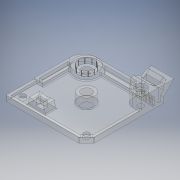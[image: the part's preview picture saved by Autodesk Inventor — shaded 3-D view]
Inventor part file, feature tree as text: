
AUTODESK INVENTOR PART (.ipt)
format: ipt  version: 2017 (Build 210142000, 142)  size: 582,144 bytes
history: native  units: in
note: dims shown in document units (in); Inventor stores cm internally (conversion verified against a paired STEP export)
features: extrude x21, sketch x21, projected_geometry x5, chamfer x3, fillet x3, pattern_circular x1
ambient origin geometry x8: Origin, YZ Plane, XZ Plane, XY Plane, X Axis, Y Axis, Z Axis, Center Point
bodies: Solid1 (feature_tree)
feature tree (54):
  extrude  "Extrusion1"  Depth=1.7323in
  chamfer  "Chamfer2"  Distance=0.1181in
  extrude  "Extrusion2"  Depth=0.1772in TaperAngle=45.0deg
  extrude  "Extrusion3"  Depth=0.1969in
  extrude  "Extrusion4"  Depth=0.815in
  extrude  "Extrusion5"  Depth=0.5118in
  extrude  "Extrusion6"  Depth=0.0787in
  fillet  "Fillet3"  Radius=0.1142in
  pattern_circular  "Circular Pattern1"  Count=10 Angle=360.0deg
  fillet  "Fillet4"  Radius=0.2953in
  extrude  "Extrusion7"  Depth=0.0591in
  extrude  "Extrusion8"  Depth=0.0591in
  extrude  "Extrusion9"  Depth=0.0394in
  extrude  "Extrusion10"  Depth=0.0984in
  extrude  "Extrusion11"  Depth=0.0591in
  chamfer  "Chamfer3"  Distance=0.0591in
  chamfer  "Chamfer4"  Distance=0.0591in
  extrude  "Extrusion12"  Depth=0.0591in
  extrude  "Extrusion13"  Depth=0.0591in
  extrude  "Extrusion14"  Depth=0.0591in TaperAngle=0.0deg
  extrude  "Extrusion15"  Depth=0.1575in
  extrude  "Extrusion16"  Depth=0.2165in TaperAngle=0.0deg
  extrude  "Extrusion17"  Depth=0.1417in
  extrude  "Extrusion18"  Depth=0.1575in
  extrude  "Extrusion19"  Depth=0.1575in
  fillet  "Fillet5"  Radius=0.2165in
  extrude  "Extrusion20"  Depth=0.1575in
  extrude  "Extrusion21"  Depth=0.1575in
  sketch  "Sketch1"  dims[d0=1.811in d1=1.7323in]
  sketch  "Sketch3"  dims[d2=0.2205in]
  projected_geometry  "Projected Loop1"
  sketch  "Sketch4"  dims[d3=1.2205in]
  sketch  "Sketch5"  dims[d4=1.2205in]
  sketch  "Sketch6"  dims[d5=0.1299in d6=0.1181in d7=0.0in]
  sketch  "Sketch7"  dims[d11=0.815in d13=0.1772in d14=0.0787in d15=45.0deg]
  sketch  "Sketch8"  dims[d16=0.1969in d17=1.1024in]
  projected_geometry  "Projected Loop2"
  sketch  "Sketch9"  dims[d18=0.2352in d19=0.815in]
  projected_geometry  "Projected Loop3"
  sketch  "Sketch10"  dims[d20=0.0197in d21=0.0in d22=0.5118in]
  sketch  "Sketch11"  dims[d23=0.0787in d24=0.0in d27=0.3622in d28=0.1142in d29=0.0in]
  sketch  "Sketch12"  dims[d30=0.2165in]
  sketch  "Sketch13"  dims[d31=0.0512in d32=0.0in]
  projected_geometry  "Projected Loop4"
  sketch  "Sketch14"  dims[d33=0.1752in]
  sketch  "Sketch15"  dims[d34=0.0118in]
  sketch  "Sketch16"  dims[d35=0.0512in d36=0.0in]
  sketch  "Sketch17"  dims[d37=0.0057in d38=3.937in d39=360.0deg d41=0.2953in]
  sketch  "Sketch18"  dims[d42=0.0728in d43=0.0591in]
  projected_geometry  "Projected Loop5"
  sketch  "Sketch19"  dims[d44=0.6417in d45=0.0591in]
  sketch  "Sketch20"  dims[d48=0.0787in d49=0.0in d50=0.0394in]
  sketch  "Sketch21"  dims[d51=0.0984in d52=0.6102in]
  sketch  "Sketch22"  dims[d53=0.0394in d54=0.0591in d55=0.0591in d56=0.0591in d57=0.0591in d58=0.0591in d59=0.0591in d60=0.0in d61=0.3543in d62=0.2165in d63=0.0in d64=0.1417in d65=0.2362in d66=0.1299in d67=0.2165in d68=0.0in d69=0.0906in d70=0.1535in d71=0.2303in d72=0.3937in d73=0.124in d74=0.5669in d75=0.1575in d76=0.0in d77=0.1575in d78=0.0787in d79=0.0687in d80=0.1575in d81=0.0787in d82=0.0687in d84=0.2411in d85=45.0deg d87=0.5118in d88=0.0in d89=0.4921in d90=0.5118in d91=0.0in d92=0.5118in d93=0.0in d96=0.3268in d97=0.1831in d98=0.0689in d99=0.0in d100=0.2352in d101=0.315in d102=0.0787in d103=0.0in d104=0.2972in d105=0.0787in d106=0.0in d107=0.248in d108=0.0827in d109=0.0in d110=0.4961in d111=0.3268in d112=0.0827in d113=0.0in d114=0.0197in d115=0.0689in d116=0.0591in d117=0.0669in d118=0.0512in d119=0.0827in d120=0.0in d121=0.1142in d122=0.0453in d124=0.0453in d125=0.0453in d126=0.0453in d127=0.0453in d130=0.0512in d131=0.0374in d132=0.0374in d133=0.0374in d134=0.0374in d136=0.0591in d137=0.0197in d138=0.1575in d139=0.0in]
